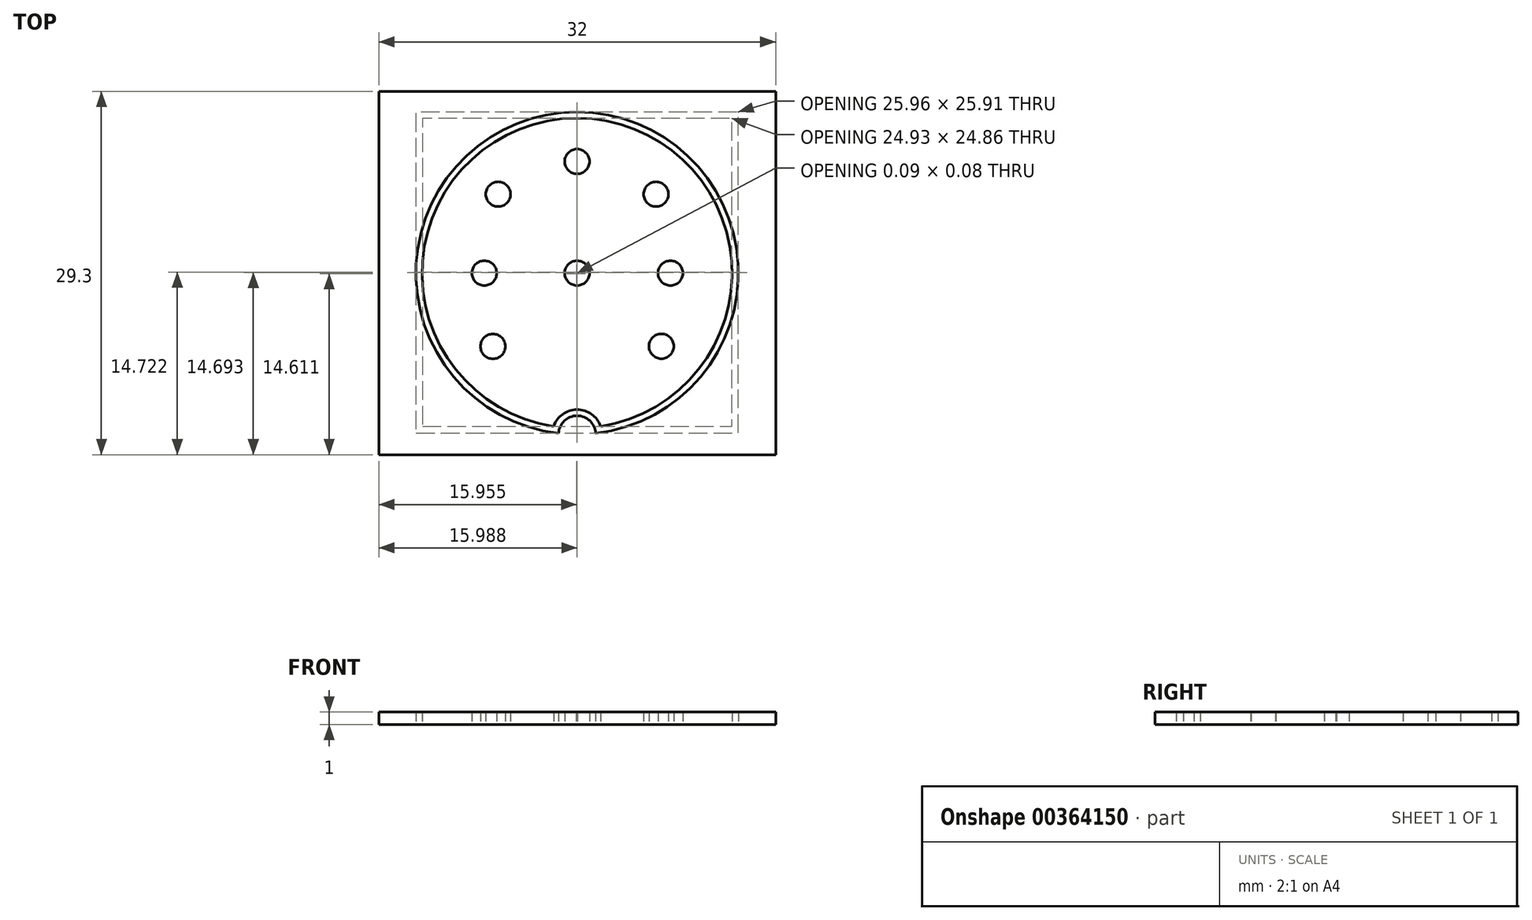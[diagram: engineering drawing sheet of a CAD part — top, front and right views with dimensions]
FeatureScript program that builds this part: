
annotation { "Feature Type Name" : "Feature", "Feature Type Description" : "" }
export const myFeature = defineFeature(function(context is Context, id is Id, definition is map)
    precondition{}
    {
        {
            var Q0;
            Q0=qCreatedBy(makeId("Top.planeOp"),FACE);
            var sketch = newSketch(context, id + "F0", { "sketchPlane" : qUnion([Q0])});
            skArc(sketch, "E0", {"start": v(1.88, -12.36) * mm, "mid": v(-0.01, 12.5) * mm, "end": v(-1.9, -12.36) * mm});
            skCircle(sketch, "E1", {"center": v(-0.01, 9) * mm, "radius": 1 * mm});
            skCircle(sketch, "E2", {"center": v(-7.5, 0) * mm, "radius": 1 * mm});
            skCircle(sketch, "E3", {"center": v(7.52, 0) * mm, "radius": 1 * mm});
            skLineSegment(sketch, "E4", {"start": v(-0.01, 0) * mm, "end": v(0, 0) * mm});
            skLineSegment(sketch, "E5", {"start": v(-0.01, 0) * mm, "end": v(-0.1, -0.08) * mm});
            skCircle(sketch, "E6", {"center": v(-6.38, 6.36) * mm, "radius": 1 * mm});
            skCircle(sketch, "E7", {"center": v(6.35, 6.37) * mm, "radius": 1 * mm});
            skArc(sketch, "E8", {"start": v(1.49, -12.91) * mm, "mid": v(-0.01, 13) * mm, "end": v(-1.5, -12.91) * mm});
            skLineSegment(sketch, "E9", {"start": v(-0.01, 0) * mm, "end": v(-0.01, -0.01) * mm});
            skArc(sketch, "E10", {"start": v(1.49, -12.91) * mm, "mid": v(-0.01, -11.5) * mm, "end": v(-1.5, -12.91) * mm});
            skArc(sketch, "E11", {"start": v(1.88, -12.36) * mm, "mid": v(-0.01, -11) * mm, "end": v(-1.9, -12.36) * mm});
            skCircle(sketch, "E12", {"center": v(-0.01, 0) * mm, "radius": 1 * mm});
            skLineSegment(sketch, "E13", {"start": v(0, 0) * mm, "end": v(-0.1, -0.08) * mm});
            skCircle(sketch, "E14", {"center": v(-6.8, -5.91) * mm, "radius": 1 * mm});
            skCircle(sketch, "E15", {"center": v(6.79, -5.9) * mm, "radius": 1 * mm});
            skLineSegment(sketch, "E16.bottom", {"start": v(16, -14.65) * mm, "end": v(-16, -14.65) * mm});
            skLineSegment(sketch, "E16.top", {"start": v(16, 14.65) * mm, "end": v(-16, 14.65) * mm});
            skLineSegment(sketch, "E16.left", {"start": v(16, -14.65) * mm, "end": v(16, 14.65) * mm});
            skLineSegment(sketch, "E16.right", {"start": v(-16, -14.65) * mm, "end": v(-16, 14.65) * mm});
            skPoint(sketch, "E16.middle", {"position": v(0, 0) * mm});
            skSolve(sketch);
        }
        {
            var Q0;
            Q0=makeQuery(id+"F0.imprint","IMPRINT",FACE,{"disambiguationData":[TD([[makeQuery(id+"F0.imprint","IMPRINT",EDGE,{"derivedFrom":sQuery(id+"F0.wireOp",EDGE,"E0")}),-1.0]])]});
            var Q1;
            Q1=makeQuery(id+"F0.imprint","IMPRINT",FACE,{"disambiguationData":[TD([[makeQuery(id+"F0.imprint","IMPRINT",EDGE,{"derivedFrom":sQuery(id+"F0.wireOp",EDGE,"E14")}),1.0]])]});
            var Q2;
            Q2=makeQuery(id+"F0.imprint","IMPRINT",FACE,{"disambiguationData":[TD([[makeQuery(id+"F0.imprint","IMPRINT",EDGE,{"derivedFrom":sQuery(id+"F0.wireOp",EDGE,"E2")}),1.0]])]});
            var Q3;
            Q3=makeQuery(id+"F0.imprint","IMPRINT",FACE,{"disambiguationData":[TD([[makeQuery(id+"F0.imprint","IMPRINT",EDGE,{"derivedFrom":sQuery(id+"F0.wireOp",EDGE,"E6")}),1.0]])]});
            var Q4;
            Q4=makeQuery(id+"F0.imprint","IMPRINT",FACE,{"disambiguationData":[TD([[makeQuery(id+"F0.imprint","IMPRINT",EDGE,{"derivedFrom":sQuery(id+"F0.wireOp",EDGE,"E1")}),1.0]])]});
            var Q5;
            Q5=makeQuery(id+"F0.imprint","IMPRINT",FACE,{"disambiguationData":[TD([[makeQuery(id+"F0.imprint","IMPRINT",EDGE,{"derivedFrom":sQuery(id+"F0.wireOp",EDGE,"E7")}),1.0]])]});
            var Q6;
            Q6=makeQuery(id+"F0.imprint","IMPRINT",FACE,{"disambiguationData":[TD([[makeQuery(id+"F0.imprint","IMPRINT",EDGE,{"derivedFrom":sQuery(id+"F0.wireOp",EDGE,"E3")}),1.0]])]});
            var Q7;
            Q7=makeQuery(id+"F0.imprint","IMPRINT",FACE,{"disambiguationData":[TD([[makeQuery(id+"F0.imprint","IMPRINT",EDGE,{"derivedFrom":sQuery(id+"F0.wireOp",EDGE,"E15")}),1.0]])]});
            var Q8;
            {var subQ2=sQuery(id+"F0.wireOp",EDGE,"E4");Q8=makeQuery(id+"F0.imprint","IMPRINT",FACE,{"disambiguationData":[TD([[makeQuery(id+"F0.imprint","IMPRINT",EDGE,{"derivedFrom":subQ2}),1.0]])]});}
            extrude(context, id + "F1", {"entities" : qUnion([Q0, Q1, Q2, Q3, Q4, Q5, Q6, Q7, Q8]), "depth" : 1 * mm});
        }
        {
            var Q0;
            Q0=makeQuery(id+"F0.imprint","IMPRINT",FACE,{"disambiguationData":[TD([[makeQuery(id+"F0.imprint","IMPRINT",EDGE,{"derivedFrom":sQuery(id+"F0.wireOp",EDGE,"E8")}),-1.0]])]});
            extrude(context, id + "F2", {"entities" : qUnion([Q0]), "depth" : 1 * mm});
        }
    });
